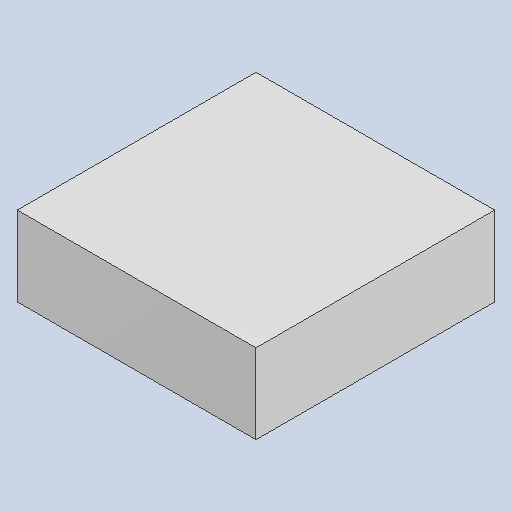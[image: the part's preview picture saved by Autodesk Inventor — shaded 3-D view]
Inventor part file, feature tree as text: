
AUTODESK INVENTOR PART (.ipt)
format: ipt  version: 2023.4 (Build 274418000, 418)  size: 79,872 bytes
history: native  units: mm
features: extrude x1
ambient origin geometry x8: Origin, YZ Plane, XZ Plane, XY Plane, X Axis, Y Axis, Z Axis, Center Point
bodies: Solid1 (feature_tree)
feature tree (1):
  extrude  "Extruded_42"  [1 undecoded]
note: 1 required parameter value undecoded (feature->parameter linkage not recoverable at this tier; creation-order binding heuristic only, values carry confidence <= 0.55)
